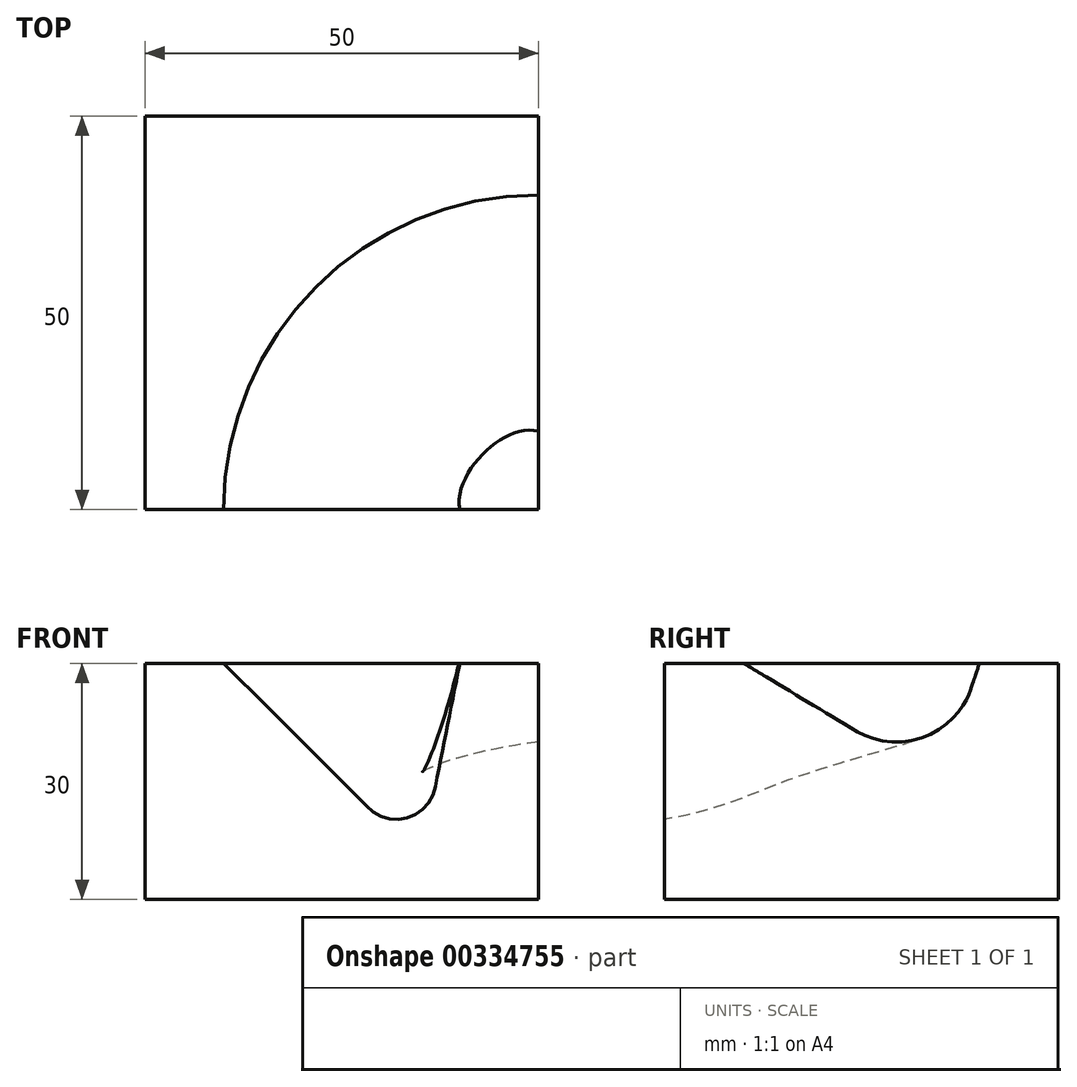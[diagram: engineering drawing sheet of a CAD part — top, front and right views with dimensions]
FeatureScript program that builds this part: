
annotation { "Feature Type Name" : "Feature", "Feature Type Description" : "" }
export const myFeature = defineFeature(function(context is Context, id is Id, definition is map)
    precondition{}
    {
        {
            var Q0;
            Q0=qCreatedBy(makeId("Top.planeOp"),FACE);
            var sketch = newSketch(context, id + "F0", { "sketchPlane" : qUnion([Q0])});
            skLineSegment(sketch, "E0.bottom", {"start": v(25, -25) * mm, "end": v(-25, -25) * mm});
            skLineSegment(sketch, "E0.top", {"start": v(25, 25) * mm, "end": v(-25, 25) * mm});
            skLineSegment(sketch, "E0.left", {"start": v(25, -25) * mm, "end": v(25, 25) * mm});
            skLineSegment(sketch, "E0.right", {"start": v(-25, -25) * mm, "end": v(-25, 25) * mm});
            skPoint(sketch, "E0.middle", {"position": v(0, 0) * mm});
            skSolve(sketch);
        }
        {
            var Q0;
            Q0=makeQuery(id+"F0.imprint","IMPRINT",FACE,{"disambiguationData":[TD([[makeQuery(id+"F0.imprint","IMPRINT",EDGE,{"derivedFrom":sQuery(id+"F0.wireOp",EDGE,"E0.bottom")}),-1.0]])]});
            extrude(context, id + "F1", {"entities" : qUnion([Q0]), "depth" : 30 * mm});
        }
        {
            var Q0;
            Q0=makeQuery(id+"F1.opExtrude","SWEPT_FACE",FACE,{"disambiguationData":[OSD([sQuery(id+"F0.wireOp",EDGE,"E0.left")])]});
            var sketch = newSketch(context, id + "F2", { "sketchPlane" : qUnion([Q0])});
            skLineSegment(sketch, "E1", {"start": v(-15, 30) * mm, "end": v(-0.69, 21.41) * mm});
            skLineSegment(sketch, "E2", {"start": v(13.94, 26.83) * mm, "end": v(15, 30) * mm});
            skPoint(sketch, "E3.visualSharp", {"position": v(10, 15) * mm});
            skArc(sketch, "E3.filletArc", {"start": v(-0.69, 21.41) * mm, "mid": v(7.92, 20.6) * mm, "end": v(13.94, 26.83) * mm});
            skSolve(sketch);
        }
        {
            var Q0;
            Q0=makeQuery(id+"F1.opExtrude","SWEPT_FACE",FACE,{"disambiguationData":[OSD([sQuery(id+"F0.wireOp",EDGE,"E0.bottom")])]});
            var sketch = newSketch(context, id + "F3", { "sketchPlane" : qUnion([Q0])});
            skLineSegment(sketch, "E4", {"start": v(-15, 30) * mm, "end": v(3.4, 11.6) * mm});
            skLineSegment(sketch, "E5", {"start": v(11.83, 14.16) * mm, "end": v(15, 30) * mm});
            skPoint(sketch, "E6.visualSharp", {"position": v(10, 5) * mm});
            skArc(sketch, "E6.filletArc", {"start": v(3.4, 11.6) * mm, "mid": v(8.38, 10.36) * mm, "end": v(11.83, 14.16) * mm});
            skSolve(sketch);
        }
        {
            var Q0;
            Q0=makeQuery(id+"F1.opExtrude","CAP_FACE",FACE,{"disambiguationData":[OSD([sQuery(id+"F0.wireOp",EDGE,"E0.bottom"),sQuery(id+"F0.wireOp",EDGE,"E0.top"),sQuery(id+"F0.wireOp",EDGE,"E0.left"),sQuery(id+"F0.wireOp",EDGE,"E0.right")])],"isStart":false});
            var sketch = newSketch(context, id + "F4", { "sketchPlane" : qUnion([Q0])});
            skCircle(sketch, "E7", {"center": v(25, -25) * mm, "radius": 10 * mm});
            skCircle(sketch, "E8", {"center": v(25, -25) * mm, "radius": 40 * mm});
            skSolve(sketch);
        }
        {
            var Q1;
            {var subQ0=sQuery(id+"F2.wireOp",EDGE,"E1");Q1=makeQuery(id+"F2.imprint","IMPRINT",FACE,{"disambiguationData":[TD([[makeQuery(id+"F2.imprint","IMPRINT",EDGE,{"derivedFrom":subQ0}),1.0]])]});}
            var Q2;
            {var subQ0=sQuery(id+"F3.wireOp",EDGE,"E4");Q2=makeQuery(id+"F3.imprint","IMPRINT",FACE,{"disambiguationData":[TD([[makeQuery(id+"F3.imprint","IMPRINT",EDGE,{"derivedFrom":subQ0}),1.0]])]});}
            var Q3;
            Q3=sQuery(id+"F4.wireOp",EDGE,"E8");
            loft(context, id + "F5", {"operationType" : NewBodyOperationType.REMOVE, "addGuides" : true, "sheetProfilesArray" : [{ "sheetProfileEntities" : qUnion([Q1]) }, { "sheetProfileEntities" : qUnion([Q2]) }], "guidesArray" : [{ "guideEntities" : qUnion([Q3]), "guideDerivativeType" : LoftGuideDerivativeType.DEFAULT, "guideDerivativeMagnitude" : 1 }]});
        }
    });
